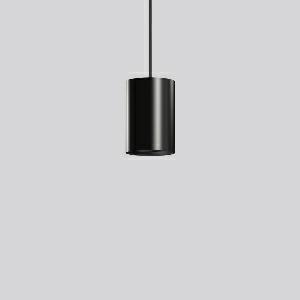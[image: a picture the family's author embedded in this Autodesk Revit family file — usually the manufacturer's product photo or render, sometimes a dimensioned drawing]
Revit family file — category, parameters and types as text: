
# Revit family: deecos_p_maxi_911539_003_fb50
name_source: partatom
category: Lighting Fixtures
units: mm (PartAtom-declared; Revit-internal decimal feet)

## family parameters
Cut with Voids When Loaded = No
Host = Face
Light Source = No
Part Type = Normal
Room Calculation Point = No
Round Connector Dimension = Use Diameter
Shared = No

## types (1)
- DEECOS P maxi (1 x LED Modul 930, 4150 lm, 3000)
    Apparent Load = 35 VA
    Approval mark = CE
    CIE Flux Codes = 97 100 100 100 100
    Color Rendering = 90
    Color Temperature = 3000
    Default Elevation = 1800 mm
    Description = Series: DEECOS P maxi
Cylindrical pendant luminaire. Housing: die-cast aluminium, powder-coated. Canopy made of powder-coated sheet steel with magnetic attachment. Optical assembly with reflector made of MIRO-Silver with 98% total light reflection for outstanding efficiency - can be changed without tools. Best colour rendering index Ra>90. Transparent suspension cable 2 m, can be shortened. High quality converter without flickering and stroboscopic effect. The following accessories can be mounted without use of tools: interchangeable lenses, honeycomb louvre, clear and frosted diffusers, white interchangeable plastic ring. Decorative recessed suspension set available as accessory. 
Colour: deep black, matt (RAL 9005)
Diameter: 123 mm
Height: 181 mm
Suspension length: 2000 mm
Lamp: LED
Socket: without socket
Colour temperature: 3000K
Colour rendering index (CRI): 92
System power: 35 W
Rated luminous flux: 4150 lm
Luminous efficiency: 119 lm/W
Control gear: Regulated power supply
Protection class: I
Type of protection: IP 20
    Height = 181 mm
    Lamp = 1 x LED Modul 930
    Lamp Light Flux = 4150 lm
    Lamp count = 1
    Length = 123 mm
    Lifetime = 50000 h
    Luminous efficacy = 119 lm/W
    Manufacturer = RZB
    ModVariant = No
    Model = 911539.003
    Mounting Place = Ceiling
    Mounting Type = Pendant
    Number of Poles = 1
    OnlyDefault = Yes
    Power Factor = 1
    Product Name = DEECOS P maxi
    Product group = Pendant luminaires
    ProductGroupID = 902
    Protection Class = Protection class I
    Protection Degree = IP 20
    RLX_Detail_Level = 1
    RLX_Emergency_Light_Flux = 0 lm
    RLX_Emergency_Type = 0
    RLX_Emergency_Type_DB = No
    RlxData = <blob elided: 36273 chars, md5=1ce8f8dc>
    Socket = socket
    Standby Power = 0 W
    System Light Flux = 4150 lm
    System Power = 35 W
    Type Comments = Product without accessories
    Type Image = 911480.003.jpg
    URL = http://relux.com
    VarID = ---
    Voltage = 230 V
    Voltage Range = 220-240 V
    Weight = 0.00 kg
    Width = 0 mm  [stored 0 ft]

note: [stored X ft] marks values corroborated as IEEE doubles in the binary element streams (Revit-internal decimal feet)

## geometry (parser evidence)
native form markers: Blend x4, Sweep x9
no freeform markers — native parametric forms only
